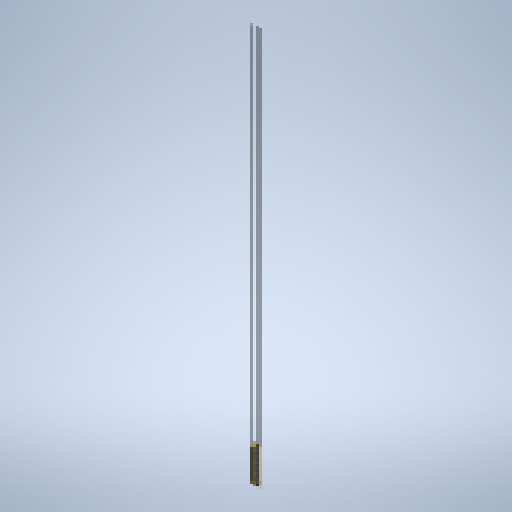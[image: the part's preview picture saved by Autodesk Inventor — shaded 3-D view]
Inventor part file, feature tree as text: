
AUTODESK INVENTOR PART (.ipt)
format: ipt  version: 2025.2 (Build 292293000, 293)  size: 334,848 bytes
history: native  units: mm
features: other x4, extrude x2, sketch x2, pattern_linear x1
ambient origin geometry x8: Origin, YZ Plane, XZ Plane, XY Plane, X Axis, Y Axis, Z Axis, Center Point
bodies: Solid1 (feature_tree)
feature tree (9):
  other  "Annotations"
  extrude  "Extrusion1"  Depth=161.0mm TaperAngle=0.0deg
  extrude  "Extrusion2"  Depth=10.0mm
  pattern_linear  "Rectangular Pattern1"  Count1=200 Spacing1=7.5mm
  sketch  "Sketch_2"  dims[d0=161.0mm d1=0.0mm d2=1.0mm d3=0.0mm]
  sketch  "Sketch_6"  dims[d4=800.0mm d6=23.0mm d7=10.0mm d9=0.0mm d13=12.0mm d10=2000.0mm d11=7.5mm d12=35.0mm]
  other  "Linear Dimension 1"
  other  "Linear Dimension 2"
  other  "Linear Dimension 3"
